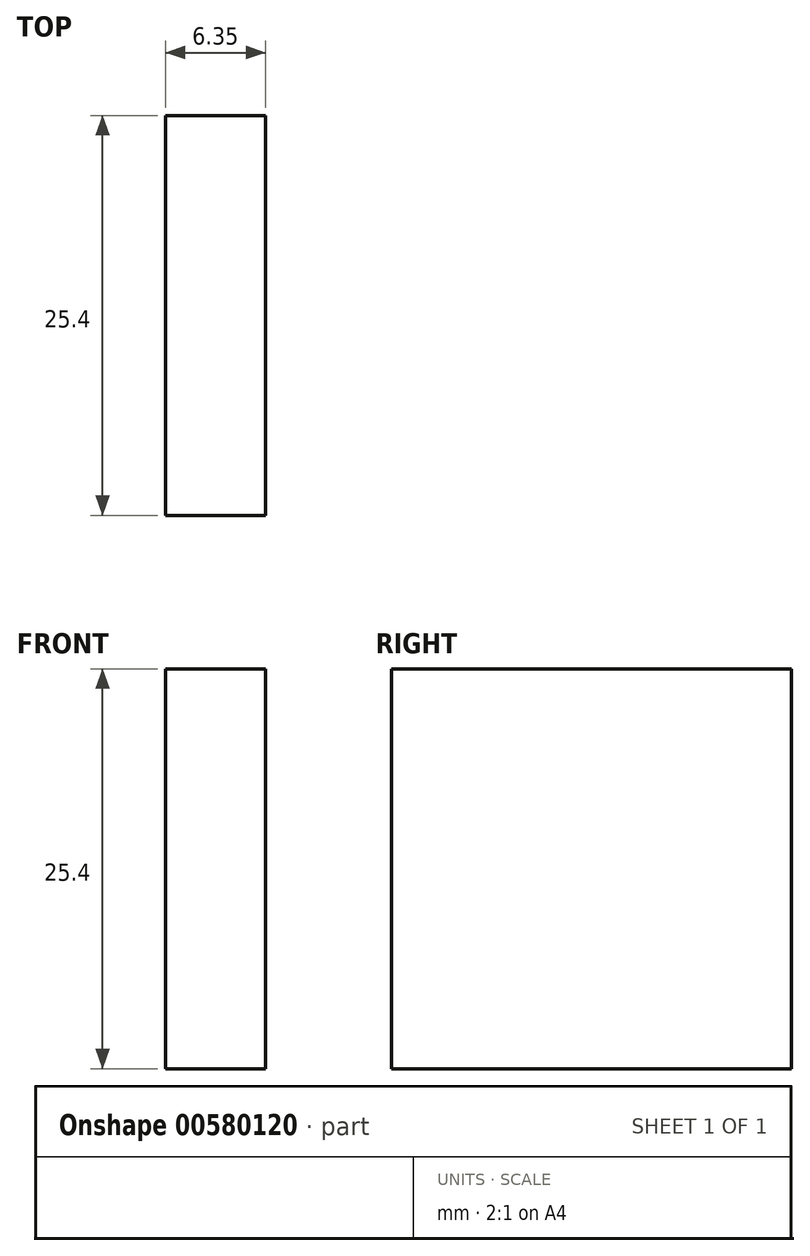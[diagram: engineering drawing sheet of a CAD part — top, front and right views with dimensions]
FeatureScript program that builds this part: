
annotation { "Feature Type Name" : "Feature", "Feature Type Description" : "" }
export const myFeature = defineFeature(function(context is Context, id is Id, definition is map)
    precondition{}
    {
        {
            var Q0;
            Q0=qCreatedBy(makeId("Right.planeOp"),FACE);
            var sketch = newSketch(context, id + "F0", { "sketchPlane" : qUnion([Q0])});
            skLineSegment(sketch, "E0.bottom", {"start": v(12.7, 12.7) * mm, "end": v(-12.7, 12.7) * mm});
            skLineSegment(sketch, "E0.top", {"start": v(12.7, -12.7) * mm, "end": v(-12.7, -12.7) * mm});
            skLineSegment(sketch, "E0.left", {"start": v(12.7, 12.7) * mm, "end": v(12.7, -12.7) * mm});
            skLineSegment(sketch, "E0.right", {"start": v(-12.7, 12.7) * mm, "end": v(-12.7, -12.7) * mm});
            skPoint(sketch, "E0.middle", {"position": v(0, 0) * mm});
            skSolve(sketch);
        }
        {
            var Q0;
            Q0=makeQuery(id+"F0.imprint","IMPRINT",FACE,{"disambiguationData":[TD([[makeQuery(id+"F0.imprint","IMPRINT",EDGE,{"derivedFrom":sQuery(id+"F0.wireOp",EDGE,"E0.bottom")}),1.0]])]});
            extrude(context, id + "F1", {"entities" : qUnion([Q0]), "depth" : 6.35 * mm, "offsetDistance" : 25.4 * mm});
        }
    });
